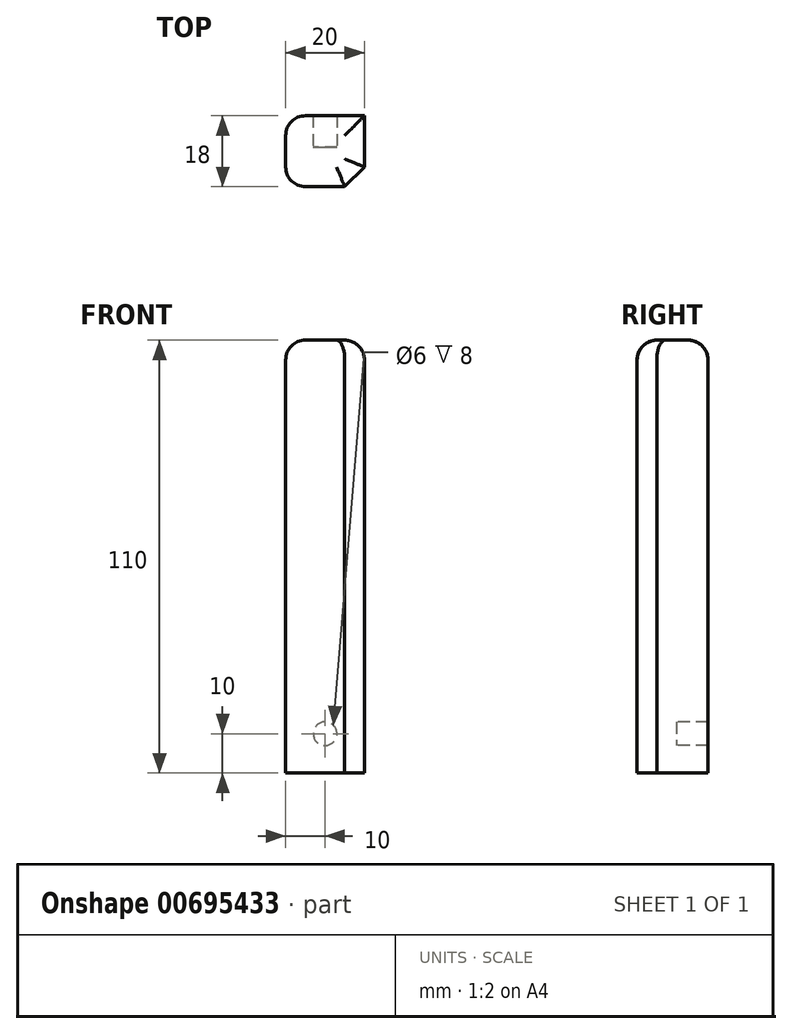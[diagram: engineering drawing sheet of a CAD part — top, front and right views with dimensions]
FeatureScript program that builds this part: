
annotation { "Feature Type Name" : "Feature", "Feature Type Description" : "" }
export const myFeature = defineFeature(function(context is Context, id is Id, definition is map)
    precondition{}
    {
        {
            var Q0;
            Q0=qCreatedBy(makeId("Front.planeOp"),FACE);
            var sketch = newSketch(context, id + "F0", { "sketchPlane" : qUnion([Q0])});
            skLineSegment(sketch, "E0.bottom", {"start": v(-10, 90) * mm, "end": v(10, 90) * mm});
            skLineSegment(sketch, "E0.top", {"start": v(-10, -10) * mm, "end": v(10, -10) * mm});
            skLineSegment(sketch, "E0.left", {"start": v(-10, 90) * mm, "end": v(-10, -10) * mm});
            skLineSegment(sketch, "E0.right", {"start": v(10, 90) * mm, "end": v(10, -10) * mm});
            skSolve(sketch);
        }
        {
            var Q0;
            Q0=makeQuery(id+"F0.imprint","IMPRINT",FACE,{"disambiguationData":[TD([[makeQuery(id+"F0.imprint","IMPRINT",EDGE,{"derivedFrom":sQuery(id+"F0.wireOp",EDGE,"E0.bottom")}),-1.0]])]});
            extrude(context, id + "F1", {"entities" : qUnion([Q0]), "depth" : 10 * mm, "offsetDistance" : 25 * mm});
        }
        {
            var Q0;
            Q0=makeQuery(id+"F1.opExtrude","CAP_FACE",FACE,{"disambiguationData":[OSD([sQuery(id+"F0.wireOp",EDGE,"E0.bottom"),sQuery(id+"F0.wireOp",EDGE,"E0.top"),sQuery(id+"F0.wireOp",EDGE,"E0.left"),sQuery(id+"F0.wireOp",EDGE,"E0.right")])],"isStart":true});
            var sketch = newSketch(context, id + "F2", { "sketchPlane" : qUnion([Q0])});
            skCircle(sketch, "E1", {"center": v(0, 0) * mm, "radius": 3 * mm});
            skSolve(sketch);
        }
        {
            var Q0;
            Q0=makeQuery(id+"F2.imprint","IMPRINT",FACE,{"disambiguationData":[TD([[makeQuery(id+"F2.imprint","IMPRINT",EDGE,{"derivedFrom":sQuery(id+"F2.wireOp",EDGE,"E1")}),-1.0]])]});
            extrude(context, id + "F3", {"entities" : qUnion([Q0]), "operationType" : NewBodyOperationType.ADD, "depth" : 8 * mm, "offsetDistance" : 25 * mm});
        }
        {
            var Q0;
            Q0=makeQuery(id+"F1.opExtrude","CAP_EDGE",EDGE,{"disambiguationData":[OSD([sQuery(id+"F0.wireOp",EDGE,"E0.right")])],"isStart":false});
            chamfer(context, id + "F4", {"entities" : qUnion([Q0]), "width" : 5 * mm, "tangentPropagation" : true});
        }
        {
            var Q0;
            Q0=makeQuery(id+"F1.opExtrude","CAP_EDGE",EDGE,{"disambiguationData":[OSD([sQuery(id+"F0.wireOp",EDGE,"E0.left")])],"isStart":false});
            var Q1;
            Q1=makeQuery(id+"F3.opExtrude","CAP_EDGE",EDGE,{"disambiguationData":[OSD([sQuery(id+"F0.wireOp",EDGE,"E0.left")])],"isStart":false});
            fillet(context, id + "F5", {"entities" : qUnion([Q0, Q1]), "radius" : 5 * mm, "tangentPropagation" : true, "allowEdgeOverflow" : false});
        }
        {
            var Q0;
            {var subQ0=sQuery(id+"F0.wireOp",EDGE,"E0.bottom");Q0=makeQuery(id+"F3.boolean.opBoolean","MERGE",FACE,{"derivedFrom":[makeQuery(id+"F1.opExtrude","SWEPT_FACE",FACE,{"disambiguationData":[OSD([subQ0])]}),makeQuery(id+"F3.opExtrude","SWEPT_FACE",FACE,{"disambiguationData":[OSD([subQ0])]})]});}
            extrude(context, id + "F6", {"entities" : qUnion([Q0]), "operationType" : NewBodyOperationType.ADD, "depth" : 10 * mm, "offsetDistance" : 25 * mm});
        }
        {
            var Q0;
            {var subQ0=sQuery(id+"F0.wireOp",EDGE,"E0.left");var subQ1=sQuery(id+"F0.wireOp",EDGE,"E0.bottom");Q0=makeQuery(id+"F6.opExtrude","CAP_EDGE",EDGE,{"disambiguationData":[OSD([subQ1,subQ0]),TDD([makeQuery(id+"F3.boolean.opBoolean","MERGE",EDGE,{"derivedFrom":[makeQuery(id+"F1.opExtrude","SWEPT_EDGE",EDGE,{"disambiguationData":[OSD([subQ1,subQ0])]}),makeQuery(id+"F3.opExtrude","SWEPT_EDGE",EDGE,{"disambiguationData":[OSD([subQ1,subQ0])]})]})])],"isStart":false});}
            var Q1;
            {var subQ0=sQuery(id+"F0.wireOp",EDGE,"E0.right");var subQ1=sQuery(id+"F0.wireOp",EDGE,"E0.bottom");Q1=makeQuery(id+"F6.opExtrude","CAP_EDGE",EDGE,{"disambiguationData":[OSD([subQ1,subQ0]),TDD([makeQuery(id+"F3.boolean.opBoolean","MERGE",EDGE,{"derivedFrom":[makeQuery(id+"F1.opExtrude","SWEPT_EDGE",EDGE,{"disambiguationData":[OSD([subQ1,subQ0])]}),makeQuery(id+"F3.opExtrude","SWEPT_EDGE",EDGE,{"disambiguationData":[OSD([subQ1,subQ0])]})]})])],"isStart":false});}
            var Q2;
            {var subQ0=sQuery(id+"F0.wireOp",EDGE,"E0.bottom");var subQ1=sQuery(id+"F0.wireOp",EDGE,"E0.right");Q2=makeQuery(id+"F6.opExtrude","CAP_EDGE",EDGE,{"disambiguationData":[OSD([subQ0,subQ1]),TDD([makeQuery(id+"F4.opChamfer","BLEND_EDGE",EDGE,{"blendedFrom":[makeQuery(id+"F1.opExtrude","CAP_EDGE",EDGE,{"disambiguationData":[OSD([subQ1])],"isStart":false}),makeQuery(id+"F3.boolean.opBoolean","MERGE",FACE,{"derivedFrom":[makeQuery(id+"F1.opExtrude","SWEPT_FACE",FACE,{"disambiguationData":[OSD([subQ0])]}),makeQuery(id+"F3.opExtrude","SWEPT_FACE",FACE,{"disambiguationData":[OSD([subQ0])]})]})],"blendedInto":[makeQuery(id+"F3.boolean.opBoolean","MERGE",FACE,{"derivedFrom":[makeQuery(id+"F1.opExtrude","SWEPT_FACE",FACE,{"disambiguationData":[OSD([subQ0])]}),makeQuery(id+"F3.opExtrude","SWEPT_FACE",FACE,{"disambiguationData":[OSD([subQ0])]})]})]})])],"isStart":false});}
            fillet(context, id + "F7", {"entities" : qUnion([Q0, Q1, Q2]), "radius" : 5 * mm, "tangentPropagation" : true, "allowEdgeOverflow" : false});
        }
    });
